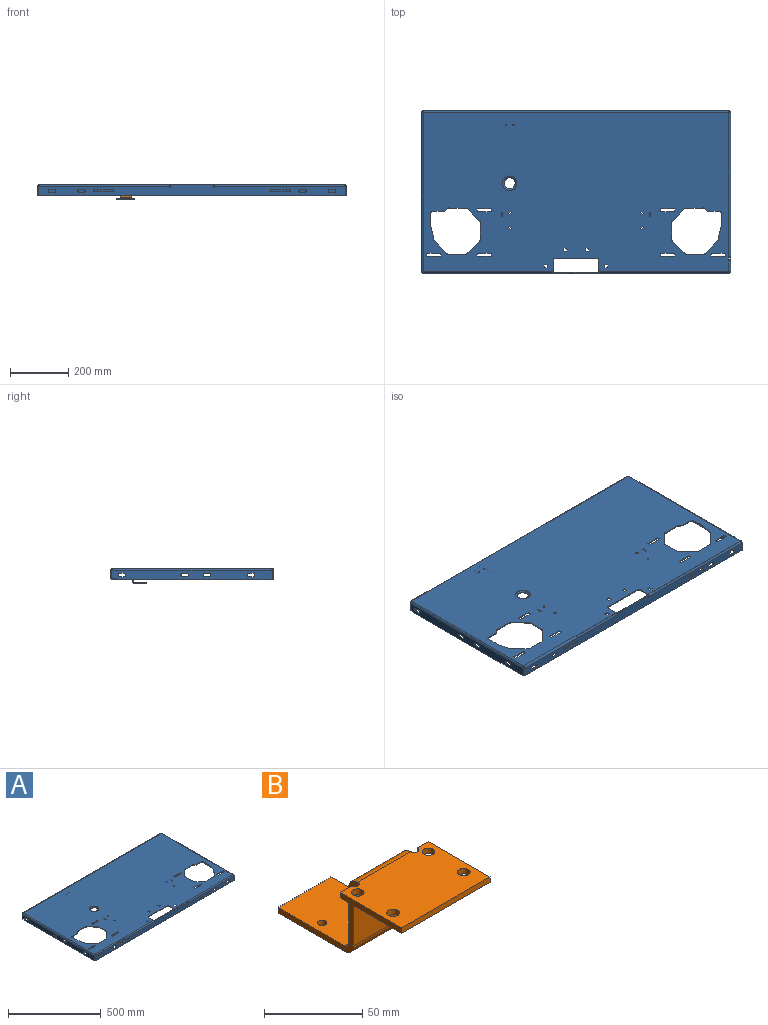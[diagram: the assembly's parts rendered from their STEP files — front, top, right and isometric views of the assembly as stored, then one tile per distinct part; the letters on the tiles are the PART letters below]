
ASSEMBLY  parts=2 mates=1
PART A: 263 faces, bbox 1066.8x558.8x38.1 mm
  f0: torus R=25.15mm, axis (0,0,-1), area 698.1mm2, adj f1,f113
  f1: plane 44.2x44.2mm, normal (0,0,-1), area 394mm2, adj f0,f2
  f2: torus R=25.15mm, axis (0,0,-1), area 1279.4mm2, adj f1,f114
  f3: plane 10.31x3.05mm, normal (0,1,0), area 31.4mm2, adj f4,f112,f113,f114
  f4: plane 10.31x3.05mm, normal (-1,0,0), area 31.4mm2, adj f3,f5,f113,f114
  f5: plane 10.31x3.05mm, normal (0,-1,0), area 31.4mm2, adj f4,f112,f113,f114
  f6: plane 3.56x3.05mm, normal (0,1,0), area 10.8mm2, adj f7,f111,f113,f114
  f7: plane 15.88x3.05mm, normal (-1,0,0), area 48.4mm2, adj f6,f8,f113,f114
  f8: plane 3.56x3.05mm, normal (0,-1,0), area 10.8mm2, adj f7,f111,f113,f114
  f9: plane 47.63x3.05mm, normal (0,1,0), area 145.2mm2, adj f10,f110,f113,f114
  f10: plane 9.91x3.05mm, normal (-1,0,0), area 30.2mm2, adj f9,f11,f113,f114
  f11: plane 47.63x3.05mm, normal (0,-1,0), area 145.2mm2, adj f10,f110,f113,f114
  f12: plane 47.63x3.05mm, normal (0,1,0), area 145.2mm2, adj f13,f109,f113,f114
  f13: plane 9.91x3.05mm, normal (-1,0,0), area 30.2mm2, adj f12,f14,f113,f114
  f14: plane 47.63x3.05mm, normal (0,-1,0), area 145.2mm2, adj f13,f109,f113,f114
  f15: plane 7.33x7.33mm, normal (-0.71,-0.71,0), area 31.6mm2, adj f16,f108,f113,f114
  f16: plane 3.38x3.38mm, normal (0.71,-0.71,0), area 14.6mm2, adj f15,f17,f113,f114
  f17: plane 7.33x7.33mm, normal (0.71,0.71,0), area 31.6mm2, adj f16,f108,f113,f114
  f18: plane 7.33x7.33mm, normal (0.71,-0.71,0), area 31.6mm2, adj f19,f107,f113,f114
  f19: plane 3.38x3.38mm, normal (0.71,0.71,0), area 14.6mm2, adj f18,f20,f113,f114
  f20: plane 7.33x7.33mm, normal (-0.71,0.71,0), area 31.6mm2, adj f19,f107,f113,f114
  f21: plane 9.91x3.05mm, normal (1,0,0), area 30.2mm2, adj f22,f106,f113,f114
  f22: plane 47.63x3.05mm, normal (0,1,0), area 145.2mm2, adj f21,f23,f113,f114
  f23: plane 9.91x3.05mm, normal (-1,0,0), area 30.2mm2, adj f22,f106,f113,f114
  f24: cylinder r=6.35mm len=6.35mm, axis (0,0,1), area 30.4mm2, adj f25,f105,f113,f114
  f25: plane 40.01x3.05mm, normal (0,-1,0), area 122mm2, adj f24,f26,f113,f114
  f26: plane 10.49x10.2mm, normal (-0.7,-0.72,0), area 44.6mm2, adj f25,f27,f113,f114
  f27: cylinder r=6.35mm len=4.52mm, axis (0,0,1), area 15.2mm2, adj f26,f28,f113,f114
  f28: plane 60.49x3.05mm, normal (0.01,-1,0), area 184.4mm2, adj f27,f29,f113,f114
  f29: cylinder r=6.35mm len=4.46mm, axis (0,0,1), area 15.2mm2, adj f28,f30,f113,f114
  f30: plane 43.38x42.17mm, normal (0.72,-0.7,0), area 184.4mm2, adj f29,f31,f113,f114
  f31: cylinder r=6.35mm len=4.52mm, axis (0,0,1), area 15.2mm2, adj f30,f32,f113,f114
  f32: plane 60.49x3.05mm, normal (1,0.01,0), area 184.4mm2, adj f31,f33,f113,f114
  f33: cylinder r=6.35mm len=4.46mm, axis (0,0,1), area 15.2mm2, adj f32,f34,f113,f114
  f34: plane 43.38x42.17mm, normal (0.7,0.72,0), area 184.4mm2, adj f33,f35,f113,f114
  f35: cylinder r=6.35mm len=4.52mm, axis (0,0,1), area 15.2mm2, adj f34,f36,f113,f114
  f36: plane 60.49x3.05mm, normal (-0.01,1,0), area 184.4mm2, adj f35,f37,f113,f114
  f37: cylinder r=6.35mm len=4.46mm, axis (0,0,1), area 15.2mm2, adj f36,f38,f113,f114
  f38: plane 43.96x42.73mm, normal (-0.72,0.7,0), area 186.9mm2, adj f37,f39,f113,f114
  f39: cylinder r=6.35mm len=3.09mm, axis (0,0,1), area 10.8mm2, adj f38,f40,f113,f114
  f40: plane 46.89x10.13mm, normal (-0.98,0.21,0), area 146.2mm2, adj f39,f41,f113,f114
  f41: cylinder r=6.35mm len=3.05mm, axis (0,0,1), area 4.1mm2, adj f40,f105,f113,f114
  f42: plane 10.31x3.05mm, normal (0,1,0), area 31.4mm2, adj f43,f104,f113,f114
  f43: plane 10.31x3.05mm, normal (-1,0,0), area 31.4mm2, adj f42,f44,f113,f114
  f44: plane 10.31x3.05mm, normal (0,-1,0), area 31.4mm2, adj f43,f104,f113,f114
  f45: plane 6.35x3.05mm, normal (1,0,0), area 19.4mm2, adj f46,f103,f113,f114
  f46: cylinder r=2.38mm len=4.76mm, axis (0,0,1), area 22.8mm2, adj f45,f113,f114,f145
  f47: plane 38.23x3.05mm, normal (-1,0,0), area 116.5mm2, adj f48,f113,f114,f258
  f48: cylinder r=6.35mm len=6.35mm, axis (0,0,1), area 30.4mm2, adj f47,f49,f113,f114
  f49: plane 142.88x3.05mm, normal (0,-1,0), area 435.5mm2, adj f48,f50,f113,f114
  f50: cylinder r=6.35mm len=6.35mm, axis (0,0,1), area 30.4mm2, adj f49,f51,f113,f114
  f51: plane 38.23x3.05mm, normal (1,0,0), area 116.5mm2, adj f50,f113,f114,f253
  f52: cylinder r=6.35mm len=4.46mm, axis (0,0,1), area 15.2mm2, adj f53,f102,f113,f114
  f53: plane 60.49x3.05mm, normal (0.01,1,0), area 184.4mm2, adj f52,f54,f113,f114
  f54: cylinder r=6.35mm len=4.52mm, axis (0,0,1), area 15.2mm2, adj f53,f55,f113,f114
  f55: plane 43.38x42.17mm, normal (-0.7,0.72,0), area 184.4mm2, adj f54,f56,f113,f114
  f56: cylinder r=6.35mm len=4.46mm, axis (0,0,1), area 15.2mm2, adj f55,f57,f113,f114
  f57: plane 60.49x3.05mm, normal (-1,0.01,0), area 184.4mm2, adj f56,f58,f113,f114
  f58: cylinder r=6.35mm len=4.52mm, axis (0,0,1), area 15.2mm2, adj f57,f59,f113,f114
  f59: plane 43.38x42.17mm, normal (-0.72,-0.7,0), area 184.4mm2, adj f58,f60,f113,f114
  f60: cylinder r=6.35mm len=4.46mm, axis (0,0,1), area 15.2mm2, adj f59,f61,f113,f114
  f61: plane 60.49x3.05mm, normal (-0.01,-1,0), area 184.4mm2, adj f60,f62,f113,f114
  f62: cylinder r=6.35mm len=4.52mm, axis (0,0,1), area 15.2mm2, adj f61,f63,f113,f114
  f63: plane 10.49x10.2mm, normal (0.7,-0.72,0), area 44.6mm2, adj f62,f64,f113,f114
  f64: plane 40.01x3.05mm, normal (0,-1,0), area 122mm2, adj f63,f65,f113,f114
  f65: cylinder r=6.35mm len=6.35mm, axis (0,0,1), area 30.4mm2, adj f64,f66,f113,f114
  f66: plane 43.19x3.05mm, normal (1,0,0), area 131.7mm2, adj f65,f67,f113,f114
  f67: cylinder r=6.35mm len=3.05mm, axis (0,0,1), area 4.1mm2, adj f66,f68,f113,f114
  f68: plane 46.89x10.13mm, normal (0.98,0.21,0), area 146.2mm2, adj f67,f69,f113,f114
  f69: cylinder r=6.35mm len=3.09mm, axis (0,0,1), area 10.8mm2, adj f68,f102,f113,f114
  f70: plane 9.91x3.05mm, normal (1,0,0), area 30.2mm2, adj f71,f101,f113,f114
  f71: plane 47.63x3.05mm, normal (0,1,0), area 145.2mm2, adj f70,f72,f113,f114
  f72: plane 9.91x3.05mm, normal (-1,0,0), area 30.2mm2, adj f71,f101,f113,f114
  f73: plane 10.31x3.05mm, normal (0,1,0), area 31.4mm2, adj f74,f100,f113,f114
  f74: plane 10.31x3.05mm, normal (-1,0,0), area 31.4mm2, adj f73,f75,f113,f114
  f75: plane 10.31x3.05mm, normal (0,-1,0), area 31.4mm2, adj f74,f100,f113,f114
  f76: plane 15.88x3.05mm, normal (1,0,0), area 48.4mm2, adj f77,f99,f113,f114
  f77: plane 3.56x3.05mm, normal (0,1,0), area 10.8mm2, adj f76,f78,f113,f114
  f78: plane 15.88x3.05mm, normal (-1,0,0), area 48.4mm2, adj f77,f99,f113,f114
  f79: plane 9.91x3.05mm, normal (1,0,0), area 30.2mm2, adj f80,f98,f113,f114
  f80: plane 47.63x3.05mm, normal (0,1,0), area 145.2mm2, adj f79,f81,f113,f114
  f81: plane 9.91x3.05mm, normal (-1,0,0), area 30.2mm2, adj f80,f98,f113,f114
  f82: plane 7.33x7.33mm, normal (0.71,0.71,0), area 31.6mm2, adj f83,f97,f113,f114
  f83: plane 3.38x3.38mm, normal (-0.71,0.71,0), area 14.6mm2, adj f82,f84,f113,f114
  f84: plane 7.33x7.33mm, normal (-0.71,-0.71,0), area 31.6mm2, adj f83,f97,f113,f114
  f85: plane 47.63x3.05mm, normal (0,1,0), area 145.2mm2, adj f86,f96,f113,f114
  f86: plane 9.91x3.05mm, normal (-1,0,0), area 30.2mm2, adj f85,f87,f113,f114
  f87: plane 47.63x3.05mm, normal (0,-1,0), area 145.2mm2, adj f86,f96,f113,f114
  f88: plane 7.33x7.33mm, normal (-0.71,0.71,0), area 31.6mm2, adj f89,f95,f113,f114
  f89: plane 3.38x3.38mm, normal (-0.71,-0.71,0), area 14.6mm2, adj f88,f90,f113,f114
  f90: plane 7.33x7.33mm, normal (0.71,-0.71,0), area 31.6mm2, adj f89,f95,f113,f114
  f91: plane 10.31x3.05mm, normal (0,1,0), area 31.4mm2, adj f92,f94,f113,f114
  f92: plane 10.31x3.05mm, normal (-1,0,0), area 31.4mm2, adj f91,f93,f113,f114
  f93: plane 10.31x3.05mm, normal (0,-1,0), area 31.4mm2, adj f92,f94,f113,f114
  f94: plane 10.31x3.05mm, normal (1,0,0), area 31.4mm2, adj f91,f93,f113,f114
  f95: plane 3.38x3.38mm, normal (0.71,0.71,0), area 14.6mm2, adj f88,f90,f113,f114
  f96: plane 9.91x3.05mm, normal (1,0,0), area 30.2mm2, adj f85,f87,f113,f114
  f97: plane 3.38x3.38mm, normal (0.71,-0.71,0), area 14.6mm2, adj f82,f84,f113,f114
  f98: plane 47.63x3.05mm, normal (0,-1,0), area 145.2mm2, adj f79,f81,f113,f114
  f99: plane 3.56x3.05mm, normal (0,-1,0), area 10.8mm2, adj f76,f78,f113,f114
  f100: plane 10.31x3.05mm, normal (1,0,0), area 31.4mm2, adj f73,f75,f113,f114
  f101: plane 47.63x3.05mm, normal (0,-1,0), area 145.2mm2, adj f70,f72,f113,f114
  f102: plane 43.96x42.73mm, normal (0.72,0.7,0), area 186.9mm2, adj f52,f69,f113,f114
  f103: cylinder r=2.38mm len=4.76mm, axis (0,0,1), area 22.8mm2, adj f45,f113,f114,f149
  f104: plane 10.31x3.05mm, normal (1,0,0), area 31.4mm2, adj f42,f44,f113,f114
  f105: plane 43.19x3.05mm, normal (-1,0,0), area 131.7mm2, adj f24,f41,f113,f114
  f106: plane 47.63x3.05mm, normal (0,-1,0), area 145.2mm2, adj f21,f23,f113,f114
  f107: plane 3.38x3.38mm, normal (-0.71,-0.71,0), area 14.6mm2, adj f18,f20,f113,f114
  f108: plane 3.38x3.38mm, normal (-0.71,0.71,0), area 14.6mm2, adj f15,f17,f113,f114
  f109: plane 9.91x3.05mm, normal (1,0,0), area 30.2mm2, adj f12,f14,f113,f114
  f110: plane 9.91x3.05mm, normal (1,0,0), area 30.2mm2, adj f9,f11,f113,f114
  f111: plane 15.88x3.05mm, normal (1,0,0), area 48.4mm2, adj f6,f8,f113,f114
  f112: plane 10.31x3.05mm, normal (1,0,0), area 31.4mm2, adj f3,f5,f113,f114
  f113: plane 1054.35x546.35mm, normal (0,0,-1), area 518903.5mm2, adj f0,f3,f4,f5,f6,f7,f8,f9
  f114: plane 1054.35x546.35mm, normal (0,0,1), area 518903.5mm2, adj f2,f3,f4,f5,f6,f7,f8,f9
  f115: plane 3.05x2.67mm, normal (0,0,1), area 8.1mm2, adj f116,f142,f143,f148
  f116: plane 25.53x3.05mm, normal (0,1,0), area 77.8mm2, adj f115,f117,f142,f143
  f117: plane 3.18x3.18mm, normal (0,0.71,-0.71), area 13.7mm2, adj f116,f118,f142,f143
  f118: plane 13.02x3.05mm, normal (0,0,-1), area 39.7mm2, adj f117,f119,f142,f143
  f119: plane 3.18x3.05mm, normal (0,1,0), area 9.7mm2, adj f118,f120,f142,f143
  f120: plane 535.5x3.05mm, normal (0,0,-1), area 1632.2mm2, adj f119,f121,f142,f143
  f121: plane 31.88x3.05mm, normal (0,-1,0), area 97.2mm2, adj f120,f122,f142,f143
  f122: plane 3.05x2.67mm, normal (0,0,1), area 8.1mm2, adj f121,f142,f143,f144
  f123: cylinder r=2.38mm len=4.76mm, axis (-1,0,0), area 22.8mm2, adj f124,f142,f143,f145
  f124: plane 6.35x3.05mm, normal (0,0,1), area 19.4mm2, adj f123,f141,f142,f143
  f125: cylinder r=5.56mm len=11.11mm, axis (-1,0,0), area 53.2mm2, adj f126,f140,f142,f143
  f126: plane 14.29x3.05mm, normal (0,0,1), area 43.5mm2, adj f125,f127,f142,f143
  f127: cylinder r=5.56mm len=11.11mm, axis (-1,0,0), area 53.2mm2, adj f126,f140,f142,f143
  f128: cylinder r=5.56mm len=11.11mm, axis (-1,0,0), area 53.2mm2, adj f129,f139,f142,f143
  f129: plane 14.29x3.05mm, normal (0,0,1), area 43.5mm2, adj f128,f130,f142,f143
  f130: cylinder r=5.56mm len=11.11mm, axis (-1,0,0), area 53.2mm2, adj f129,f139,f142,f143
  f131: cylinder r=5.56mm len=11.11mm, axis (-1,0,0), area 53.2mm2, adj f132,f138,f142,f143
  f132: plane 14.29x3.05mm, normal (0,0,1), area 43.5mm2, adj f131,f133,f142,f143
  f133: cylinder r=5.56mm len=11.11mm, axis (-1,0,0), area 53.2mm2, adj f132,f138,f142,f143
  f134: cylinder r=5.56mm len=11.11mm, axis (-1,0,0), area 53.2mm2, adj f135,f137,f142,f143
  f135: plane 14.29x3.05mm, normal (0,0,1), area 43.5mm2, adj f134,f136,f142,f143
  f136: cylinder r=5.56mm len=11.11mm, axis (-1,0,0), area 53.2mm2, adj f135,f137,f142,f143
  f137: plane 14.29x3.05mm, normal (0,0,-1), area 43.5mm2, adj f134,f136,f142,f143
  f138: plane 14.29x3.05mm, normal (0,0,-1), area 43.5mm2, adj f131,f133,f142,f143
  f139: plane 14.29x3.05mm, normal (0,0,-1), area 43.5mm2, adj f128,f130,f142,f143
  f140: plane 14.29x3.05mm, normal (0,0,-1), area 43.5mm2, adj f125,f127,f142,f143
  f141: cylinder r=2.38mm len=4.76mm, axis (-1,0,0), area 22.8mm2, adj f124,f142,f143,f149
  f142: plane 551.69x31.88mm, normal (-1,0,0), area 16488.9mm2, adj f115,f116,f117,f118,f119,f120,f121,f122
  f143: plane 551.69x31.88mm, normal (1,0,0), area 16488.9mm2, adj f115,f116,f117,f118,f119,f120,f121,f122
  f144: plane 6.22x6.22mm, normal (0,-1,0), area 22.5mm2, adj f122,f146,f147,f257
  f145: plane 6.22x6.22mm, normal (0,1,0), area 22.5mm2, adj f46,f123,f146,f147
  f146: cylinder r=3.17mm len=35.38mm, axis (0,-1,0), area 176.5mm2, adj f113,f142,f144,f145
  f147: cylinder r=6.22mm len=35.38mm, axis (0,-1,0), area 345.9mm2, adj f114,f143,f144,f145
  f148: plane 6.22x6.22mm, normal (0,1,0), area 22.5mm2, adj f115,f150,f151,f188
  f149: plane 6.22x6.22mm, normal (0,-1,0), area 22.5mm2, adj f103,f141,f150,f151
  f150: cylinder r=3.17mm len=495.1mm, axis (0,-1,0), area 2469.2mm2, adj f113,f142,f148,f149
  f151: cylinder r=6.22mm len=495.1mm, axis (0,-1,0), area 4839.6mm2, adj f114,f143,f148,f149
  f152: plane 25.53x3.05mm, normal (0,1,0), area 77.8mm2, adj f153,f175,f176,f177
  f153: plane 3.05x2.67mm, normal (0,0,1), area 8.1mm2, adj f152,f176,f177,f179
  f154: plane 3.05x2.67mm, normal (0,0,1), area 8.1mm2, adj f155,f176,f177,f178
  f155: plane 31.88x3.05mm, normal (0,-1,0), area 97.2mm2, adj f154,f156,f176,f177
  f156: plane 535.5x3.05mm, normal (0,0,-1), area 1632.2mm2, adj f155,f157,f176,f177
  f157: plane 3.18x3.05mm, normal (0,1,0), area 9.7mm2, adj f156,f158,f176,f177
  f158: plane 13.02x3.05mm, normal (0,0,-1), area 39.7mm2, adj f157,f175,f176,f177
  f159: cylinder r=5.56mm len=11.11mm, axis (1,0,0), area 53.2mm2, adj f160,f174,f176,f177
  f160: plane 14.29x3.05mm, normal (0,0,-1), area 43.5mm2, adj f159,f161,f176,f177
  f161: cylinder r=5.56mm len=11.11mm, axis (1,0,0), area 53.2mm2, adj f160,f174,f176,f177
  f162: cylinder r=5.56mm len=11.11mm, axis (1,0,0), area 53.2mm2, adj f163,f173,f176,f177
  f163: plane 14.29x3.05mm, normal (0,0,-1), area 43.5mm2, adj f162,f164,f176,f177
  f164: cylinder r=5.56mm len=11.11mm, axis (1,0,0), area 53.2mm2, adj f163,f173,f176,f177
  f165: cylinder r=5.56mm len=11.11mm, axis (1,0,0), area 53.2mm2, adj f166,f172,f176,f177
  f166: plane 14.29x3.05mm, normal (0,0,-1), area 43.5mm2, adj f165,f167,f176,f177
  f167: cylinder r=5.56mm len=11.11mm, axis (1,0,0), area 53.2mm2, adj f166,f172,f176,f177
  f168: cylinder r=5.56mm len=11.11mm, axis (1,0,0), area 53.2mm2, adj f169,f171,f176,f177
  f169: plane 14.29x3.05mm, normal (0,0,-1), area 43.5mm2, adj f168,f170,f176,f177
  f170: cylinder r=5.56mm len=11.11mm, axis (1,0,0), area 53.2mm2, adj f169,f171,f176,f177
  f171: plane 14.29x3.05mm, normal (0,0,1), area 43.5mm2, adj f168,f170,f176,f177
  f172: plane 14.29x3.05mm, normal (0,0,1), area 43.5mm2, adj f165,f167,f176,f177
  f173: plane 14.29x3.05mm, normal (0,0,1), area 43.5mm2, adj f162,f164,f176,f177
  f174: plane 14.29x3.05mm, normal (0,0,1), area 43.5mm2, adj f159,f161,f176,f177
  f175: plane 3.18x3.18mm, normal (0,0.71,-0.71), area 13.7mm2, adj f152,f158,f176,f177
  f176: plane 551.69x31.88mm, normal (1,0,0), area 16506.7mm2, adj f152,f153,f154,f155,f156,f157,f158,f159
  f177: plane 551.69x31.88mm, normal (-1,0,0), area 16506.7mm2, adj f152,f153,f154,f155,f156,f157,f158,f159
  f178: plane 6.22x6.22mm, normal (0,-1,0), area 22.5mm2, adj f154,f180,f181,f254
  f179: plane 6.22x6.22mm, normal (0,1,0), area 22.5mm2, adj f153,f180,f181,f189
  f180: cylinder r=3.17mm len=546.35mm, axis (0,-1,0), area 2724.8mm2, adj f113,f176,f178,f179
  f181: cylinder r=6.22mm len=546.35mm, axis (0,-1,0), area 5340.6mm2, adj f114,f177,f178,f179
  f182: plane 25.65x3.05mm, normal (1,0,0), area 78.2mm2, adj f183,f186,f187,f197
  f183: plane 3.05x2.67mm, normal (0,0,1), area 8.1mm2, adj f182,f186,f187,f188
  f184: plane 3.05x2.67mm, normal (0,0,1), area 8.1mm2, adj f185,f186,f187,f189
  f185: plane 25.65x3.05mm, normal (-1,0,0), area 78.2mm2, adj f184,f186,f187,f198
  f186: plane 1059.69x25.65mm, normal (0,-1,0), area 27185.2mm2, adj f182,f183,f184,f185,f190,f199
  f187: plane 1059.69x25.65mm, normal (0,1,0), area 27185.2mm2, adj f182,f183,f184,f185,f191,f200
  f188: plane 6.22x6.22mm, normal (1,0,0), area 22.5mm2, adj f148,f183,f190,f191
  f189: plane 6.22x6.22mm, normal (-1,0,0), area 22.5mm2, adj f179,f184,f190,f191
  f190: cylinder r=3.17mm len=1054.35mm, axis (1,0,0), area 5258.4mm2, adj f113,f186,f188,f189
  f191: cylinder r=6.22mm len=1054.35mm, axis (1,0,0), area 10306.4mm2, adj f114,f187,f188,f189
  f192: plane 1059.69x3.05mm, normal (0,-1,0), area 3229.9mm2, adj f193,f194,f195,f196
  f193: plane 12.83x3.05mm, normal (1,0,0), area 39.1mm2, adj f192,f195,f196,f197
  f194: plane 12.83x3.05mm, normal (-1,0,0), area 39.1mm2, adj f192,f195,f196,f198
  f195: plane 1059.69x12.83mm, normal (0,0,1), area 13592.6mm2, adj f192,f193,f194,f199
  f196: plane 1059.69x12.83mm, normal (0,0,-1), area 13592.6mm2, adj f192,f193,f194,f200
  f197: plane 6.22x6.22mm, normal (1,0,0), area 22.5mm2, adj f182,f193,f199,f200
  f198: plane 6.22x6.22mm, normal (-1,0,0), area 22.5mm2, adj f185,f194,f199,f200
  f199: cylinder r=3.17mm len=1059.69mm, axis (1,0,0), area 5285mm2, adj f186,f195,f197,f198
  f200: cylinder r=6.22mm len=1059.69mm, axis (1,0,0), area 10358.5mm2, adj f187,f196,f197,f198
  f201: cylinder r=3.57mm len=7.14mm, axis (0,1,0), area 34.2mm2, adj f202,f250,f251,f252
  f202: plane 11.91x3.05mm, normal (0,0,1), area 36.3mm2, adj f201,f203,f251,f252
  f203: cylinder r=3.57mm len=7.14mm, axis (0,1,0), area 34.2mm2, adj f202,f250,f251,f252
  f204: cylinder r=3.57mm len=7.14mm, axis (0,1,0), area 34.2mm2, adj f205,f249,f251,f252
  f205: plane 11.91x3.05mm, normal (0,0,1), area 36.3mm2, adj f204,f206,f251,f252
  f206: cylinder r=3.57mm len=7.14mm, axis (0,1,0), area 34.2mm2, adj f205,f249,f251,f252
  f207: plane 146.05x3.05mm, normal (0,0,1), area 445.2mm2, adj f208,f248,f251,f252
  f208: plane 6.22x3.05mm, normal (1,0,0), area 19mm2, adj f207,f209,f251,f252
  f209: cylinder r=2.38mm len=4.76mm, axis (0,1,0), area 22.8mm2, adj f208,f251,f252,f258
  f210: plane 3.05x2.67mm, normal (0,0,1), area 8.1mm2, adj f211,f251,f252,f257
  f211: plane 31.88x3.05mm, normal (1,0,0), area 97.2mm2, adj f210,f212,f251,f252
  f212: plane 1059.69x3.05mm, normal (0,0,-1), area 3229.9mm2, adj f211,f213,f251,f252
  f213: plane 31.88x3.05mm, normal (-1,0,0), area 97.2mm2, adj f212,f214,f251,f252
  f214: plane 3.05x2.67mm, normal (0,0,1), area 8.1mm2, adj f213,f251,f252,f254
  f215: cylinder r=2.38mm len=4.76mm, axis (0,1,0), area 22.8mm2, adj f248,f251,f252,f253
  f216: cylinder r=3.57mm len=7.14mm, axis (0,1,0), area 34.2mm2, adj f217,f247,f251,f252
  f217: plane 11.91x3.05mm, normal (0,0,-1), area 36.3mm2, adj f216,f218,f251,f252
  f218: cylinder r=3.57mm len=7.14mm, axis (0,1,0), area 34.2mm2, adj f217,f247,f251,f252
  f219: cylinder r=3.57mm len=7.14mm, axis (0,1,0), area 34.2mm2, adj f220,f246,f251,f252
  f220: plane 11.91x3.05mm, normal (0,0,-1), area 36.3mm2, adj f219,f221,f251,f252
  f221: cylinder r=3.57mm len=7.14mm, axis (0,1,0), area 34.2mm2, adj f220,f246,f251,f252
  f222: cylinder r=3.57mm len=7.14mm, axis (0,1,0), area 34.2mm2, adj f223,f245,f251,f252
  f223: plane 11.91x3.05mm, normal (0,0,-1), area 36.3mm2, adj f222,f224,f251,f252
  f224: cylinder r=3.57mm len=7.14mm, axis (0,1,0), area 34.2mm2, adj f223,f245,f251,f252
  f225: cylinder r=5.56mm len=11.11mm, axis (0,1,0), area 53.2mm2, adj f226,f244,f251,f252
  f226: plane 14.29x3.05mm, normal (0,0,-1), area 43.5mm2, adj f225,f227,f251,f252
  f227: cylinder r=5.56mm len=11.11mm, axis (0,1,0), area 53.2mm2, adj f226,f244,f251,f252
  f228: cylinder r=5.56mm len=11.11mm, axis (0,1,0), area 53.2mm2, adj f229,f243,f251,f252
  f229: plane 14.29x3.05mm, normal (0,0,-1), area 43.5mm2, adj f228,f230,f251,f252
  f230: cylinder r=5.56mm len=11.11mm, axis (0,1,0), area 53.2mm2, adj f229,f243,f251,f252
  f231: cylinder r=5.56mm len=11.11mm, axis (0,1,0), area 53.2mm2, adj f232,f242,f251,f252
  f232: plane 14.29x3.05mm, normal (0,0,-1), area 43.5mm2, adj f231,f233,f251,f252
  f233: cylinder r=5.56mm len=11.11mm, axis (0,1,0), area 53.2mm2, adj f232,f242,f251,f252
  f234: cylinder r=3.57mm len=7.14mm, axis (0,1,0), area 34.2mm2, adj f235,f241,f251,f252
  f235: plane 11.91x3.05mm, normal (0,0,-1), area 36.3mm2, adj f234,f236,f251,f252
  f236: cylinder r=3.57mm len=7.14mm, axis (0,1,0), area 34.2mm2, adj f235,f241,f251,f252
  f237: cylinder r=5.56mm len=11.11mm, axis (0,1,0), area 53.2mm2, adj f238,f240,f251,f252
  f238: plane 14.29x3.05mm, normal (0,0,-1), area 43.5mm2, adj f237,f239,f251,f252
  f239: cylinder r=5.56mm len=11.11mm, axis (0,1,0), area 53.2mm2, adj f238,f240,f251,f252
  f240: plane 14.29x3.05mm, normal (0,0,1), area 43.5mm2, adj f237,f239,f251,f252
  f241: plane 11.91x3.05mm, normal (0,0,1), area 36.3mm2, adj f234,f236,f251,f252
  f242: plane 14.29x3.05mm, normal (0,0,1), area 43.5mm2, adj f231,f233,f251,f252
  f243: plane 14.29x3.05mm, normal (0,0,1), area 43.5mm2, adj f228,f230,f251,f252
  f244: plane 14.29x3.05mm, normal (0,0,1), area 43.5mm2, adj f225,f227,f251,f252
  f245: plane 11.91x3.05mm, normal (0,0,1), area 36.3mm2, adj f222,f224,f251,f252
  f246: plane 11.91x3.05mm, normal (0,0,1), area 36.3mm2, adj f219,f221,f251,f252
  f247: plane 11.91x3.05mm, normal (0,0,1), area 36.3mm2, adj f216,f218,f251,f252
  f248: plane 6.22x3.05mm, normal (-1,0,0), area 19mm2, adj f207,f215,f251,f252
  f249: plane 11.91x3.05mm, normal (0,0,-1), area 36.3mm2, adj f204,f206,f251,f252
  f250: plane 11.91x3.05mm, normal (0,0,-1), area 36.3mm2, adj f201,f203,f251,f252
  f251: plane 1059.69x38.1mm, normal (0,1,0), area 32896.9mm2, adj f201,f202,f203,f204,f205,f206,f207,f208
  f252: plane 1059.69x38.1mm, normal (0,-1,0), area 32896.9mm2, adj f201,f202,f203,f204,f205,f206,f207,f208
  f253: plane 6.22x6.22mm, normal (1,0,0), area 22.5mm2, adj f51,f215,f255,f256
  f254: plane 6.22x6.22mm, normal (-1,0,0), area 22.5mm2, adj f178,f214,f255,f256
  f255: cylinder r=3.17mm len=449.39mm, axis (1,0,0), area 2241.2mm2, adj f113,f251,f253,f254
  f256: cylinder r=6.22mm len=449.39mm, axis (1,0,0), area 4392.8mm2, adj f114,f252,f253,f254
  f257: plane 6.22x6.22mm, normal (1,0,0), area 22.5mm2, adj f144,f210,f259,f260
  f258: plane 6.22x6.22mm, normal (-1,0,0), area 22.5mm2, adj f47,f209,f259,f260
  f259: cylinder r=3.17mm len=449.39mm, axis (1,0,0), area 2241.2mm2, adj f113,f251,f257,f258
  f260: cylinder r=6.22mm len=449.39mm, axis (1,0,0), area 4392.8mm2, adj f114,f252,f257,f258
  f261: cylinder r=2.38mm len=4.76mm, axis (0,0,1), area 45.6mm2, adj f113,f114
  f262: cylinder r=2.38mm len=4.76mm, axis (0,0,1), area 45.6mm2, adj f113,f114
PART B: 32 faces, bbox 63.5x101.6x47.9 mm
  f0: plane 63.5x44.22mm, normal (0,0,-1), area 2663.6mm2, adj f1,f2,f3,f4,f5,f6,f7,f8
  f1: plane 7.94x3.4mm, normal (0,1,0), area 27mm2, adj f0,f2,f11,f12
  f2: plane 44.22x3.4mm, normal (1,0,0), area 150.5mm2, adj f0,f1,f3,f12
  f3: plane 63.5x3.4mm, normal (0,-1,0), area 216.1mm2, adj f0,f2,f4,f12
  f4: plane 44.22x3.4mm, normal (-1,0,0), area 150.5mm2, adj f0,f3,f6,f12
  f5: cylinder r=2.38mm len=4.76mm, axis (0,0,-1), area 25.5mm2, adj f0,f6,f12,f29
  f6: plane 7.94x3.4mm, normal (0,1,0), area 27mm2, adj f0,f4,f5,f12
  f7: cylinder r=3.17mm len=6.35mm, axis (0,0,-1), area 67.9mm2, adj f0,f12
  f8: cylinder r=3.17mm len=6.35mm, axis (0,0,-1), area 67.9mm2, adj f0,f12
  f9: cylinder r=3.17mm len=6.35mm, axis (0,0,-1), area 67.9mm2, adj f0,f12
  f10: cylinder r=3.17mm len=6.35mm, axis (0,0,-1), area 67.9mm2, adj f0,f12
  f11: cylinder r=2.38mm len=4.76mm, axis (0,0,-1), area 25.5mm2, adj f0,f1,f12,f28
  f12: plane 63.5x44.22mm, normal (0,0,1), area 2663.6mm2, adj f1,f2,f3,f4,f5,f6,f7,f8
  f13: plane 34.7x3.4mm, normal (1,0,0), area 118.1mm2, adj f15,f16,f24,f28
  f14: plane 34.7x3.4mm, normal (-1,0,0), area 118.1mm2, adj f15,f16,f25,f29
  f15: plane 38.1x34.7mm, normal (0,-1,0), area 1321.9mm2, adj f13,f14,f26,f31
  f16: plane 38.1x34.7mm, normal (0,1,0), area 1321.9mm2, adj f13,f14,f27,f30
  f17: plane 38.1x3.4mm, normal (0,1,0), area 129.7mm2, adj f18,f21,f22,f23
  f18: plane 47.63x3.4mm, normal (1,0,0), area 162.1mm2, adj f17,f22,f23,f24
  f19: cylinder r=2.38mm len=4.76mm, axis (0,0,-1), area 50.9mm2, adj f22,f23
  f20: cylinder r=2.38mm len=4.76mm, axis (0,0,-1), area 50.9mm2, adj f22,f23
  f21: plane 47.63x3.4mm, normal (-1,0,0), area 162.1mm2, adj f17,f22,f23,f25
  f22: plane 47.63x38.1mm, normal (0,0,-1), area 1778.9mm2, adj f17,f18,f19,f20,f21,f26
  f23: plane 47.63x38.1mm, normal (0,0,1), area 1778.9mm2, adj f17,f18,f19,f20,f21,f27
  f24: plane 6.58x6.58mm, normal (1,0,0), area 26.1mm2, adj f13,f18,f26,f27
  f25: plane 6.58x6.58mm, normal (-1,0,0), area 26.1mm2, adj f14,f21,f26,f27
  f26: cylinder r=6.58mm len=38.1mm, axis (1,0,0), area 393.7mm2, adj f15,f22,f24,f25
  f27: cylinder r=3.17mm len=38.1mm, axis (1,0,0), area 190mm2, adj f16,f23,f24,f25
  f28: plane 6.58x6.58mm, normal (1,0,0), area 26.1mm2, adj f11,f13,f30,f31
  f29: plane 6.58x6.58mm, normal (-1,0,0), area 26.1mm2, adj f5,f14,f30,f31
  f30: cylinder r=6.58mm len=38.1mm, axis (1,0,0), area 393.7mm2, adj f12,f16,f28,f29
  f31: cylinder r=3.17mm len=38.1mm, axis (1,0,0), area 190mm2, adj f0,f15,f28,f29
PLACE A at identity
PLACE B rot(axis=(0,1,0),180deg) t=(-196.85,95.76,77.35)mm
MATE fastened B.f20 <-> A.f262  axis (0,0,1) through (-241.3,256.91,0)mm
